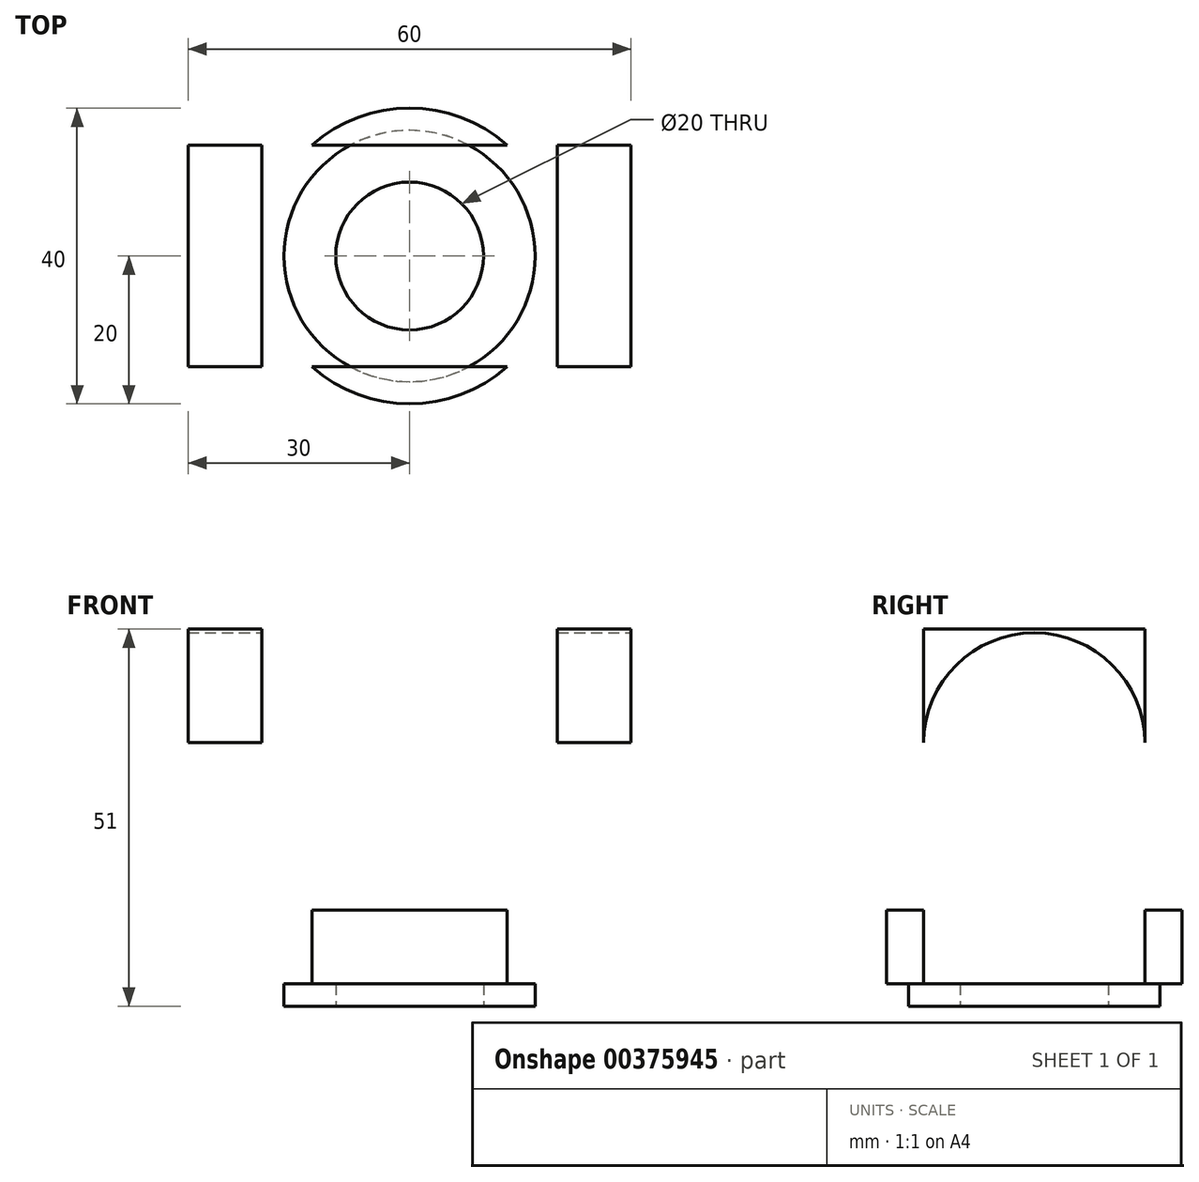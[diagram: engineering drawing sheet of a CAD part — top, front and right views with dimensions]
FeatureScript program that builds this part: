
annotation { "Feature Type Name" : "Feature", "Feature Type Description" : "" }
export const myFeature = defineFeature(function(context is Context, id is Id, definition is map)
    precondition{}
    {
        {
            var Q0;
            Q0=qCreatedBy(makeId("Top.planeOp"),FACE);
            var sketch = newSketch(context, id + "F0", { "sketchPlane" : qUnion([Q0])});
            skCircle(sketch, "E0", {"center": v(0, 0) * mm, "radius": 10 * mm});
            skCircle(sketch, "E1", {"center": v(0, 0) * mm, "radius": 20 * mm});
            skLineSegment(sketch, "E2.bottom", {"start": v(30, 15) * mm, "end": v(-30, 15) * mm});
            skLineSegment(sketch, "E2.top", {"start": v(30, -15) * mm, "end": v(-30, -15) * mm});
            skLineSegment(sketch, "E2.left", {"start": v(30, 15) * mm, "end": v(30, -15) * mm});
            skLineSegment(sketch, "E2.right", {"start": v(-30, 15) * mm, "end": v(-30, -15) * mm});
            skCircle(sketch, "E3", {"center": v(0, 0) * mm, "radius": 17 * mm});
            skSolve(sketch);
        }
        {
            var Q0;
            {var subQ5=sQuery(id+"F0.wireOp",EDGE,"E2.left");Q0=makeQuery(id+"F0.imprint","IMPRINT",FACE,{"disambiguationData":[TD([[makeQuery(id+"F0.imprint","IMPRINT",EDGE,{"derivedFrom":subQ5}),-1.0]])]});}
            var Q1;
            {var subQ5=sQuery(id+"F0.wireOp",EDGE,"E2.right");Q1=makeQuery(id+"F0.imprint","IMPRINT",FACE,{"disambiguationData":[TD([[makeQuery(id+"F0.imprint","IMPRINT",EDGE,{"derivedFrom":subQ5}),1.0]])]});}
            var Q2;
            {var subQ0=sQuery(id+"F0.wireOp",EDGE,"E2.bottom");var subQ1=sQuery(id+"F0.wireOp",EDGE,"E1");var subQ2=makeQuery(id+"F0.imprint","INTERSECT",VERTEX,{"disambiguationData":[OD(0.0)],"derivedFrom":[subQ1,subQ0]});Q2=makeQuery(id+"F0.imprint","IMPRINT",FACE,{"disambiguationData":[TD([[makeQuery(id+"F0.imprint","IMPRINT",EDGE,{"disambiguationData":[TD([[subQ2,1.0]])],"derivedFrom":subQ1}),1.0]])]});}
            var Q3;
            {var subQ0=sQuery(id+"F0.wireOp",EDGE,"E2.top");var subQ1=sQuery(id+"F0.wireOp",EDGE,"E1");var subQ2=makeQuery(id+"F0.imprint","INTERSECT",VERTEX,{"disambiguationData":[OD(0.0)],"derivedFrom":[subQ1,subQ0]});Q3=makeQuery(id+"F0.imprint","IMPRINT",FACE,{"disambiguationData":[TD([[makeQuery(id+"F0.imprint","IMPRINT",EDGE,{"disambiguationData":[TD([[subQ2,-1.0]])],"derivedFrom":subQ1}),1.0]])]});}
            var Q4;
            {var subQ0=sQuery(id+"F0.wireOp",EDGE,"E2.bottom");var subQ1=sQuery(id+"F0.wireOp",EDGE,"E1");var subQ2=makeQuery(id+"F0.imprint","INTERSECT",VERTEX,{"disambiguationData":[OD(1.0)],"derivedFrom":[subQ1,subQ0]});Q4=makeQuery(id+"F0.imprint","IMPRINT",FACE,{"disambiguationData":[TD([[makeQuery(id+"F0.imprint","IMPRINT",EDGE,{"disambiguationData":[TD([[subQ2,1.0]])],"derivedFrom":subQ1}),1.0]])]});}
            var Q5;
            {var subQ0=sQuery(id+"F0.wireOp",EDGE,"E2.bottom");var subQ1=sQuery(id+"F0.wireOp",EDGE,"E1");var subQ2=makeQuery(id+"F0.imprint","INTERSECT",VERTEX,{"disambiguationData":[OD(0.0)],"derivedFrom":[subQ1,subQ0]});Q5=makeQuery(id+"F0.imprint","IMPRINT",FACE,{"disambiguationData":[TD([[makeQuery(id+"F0.imprint","IMPRINT",EDGE,{"disambiguationData":[TD([[subQ2,-1.0]])],"derivedFrom":subQ1}),1.0]])]});}
            var Q6;
            Q6=makeQuery(id+"F0.imprint","IMPRINT",FACE,{"disambiguationData":[TD([[makeQuery(id+"F0.imprint","IMPRINT",EDGE,{"derivedFrom":sQuery(id+"F0.wireOp",EDGE,"E0")}),-1.0]])]});
            var Q7;
            {var subQ0=sQuery(id+"F0.wireOp",EDGE,"E3");var subQ1=sQuery(id+"F0.wireOp",EDGE,"E2.bottom");var subQ2=makeQuery(id+"F0.imprint","INTERSECT",VERTEX,{"disambiguationData":[OD(0.0)],"derivedFrom":[subQ1,subQ0]});Q7=makeQuery(id+"F0.imprint","IMPRINT",FACE,{"disambiguationData":[TD([[makeQuery(id+"F0.imprint","IMPRINT",EDGE,{"disambiguationData":[TD([[subQ2,-1.0]])],"derivedFrom":subQ1}),-1.0]])]});}
            var Q8;
            {var subQ0=sQuery(id+"F0.wireOp",EDGE,"E3");var subQ1=sQuery(id+"F0.wireOp",EDGE,"E2.top");var subQ2=makeQuery(id+"F0.imprint","INTERSECT",VERTEX,{"disambiguationData":[OD(0.0)],"derivedFrom":[subQ1,subQ0]});Q8=makeQuery(id+"F0.imprint","IMPRINT",FACE,{"disambiguationData":[TD([[makeQuery(id+"F0.imprint","IMPRINT",EDGE,{"disambiguationData":[TD([[subQ2,-1.0]])],"derivedFrom":subQ1}),1.0]])]});}
            extrude(context, id + "F1", {"entities" : qUnion([Q0, Q1, Q2, Q3, Q4, Q5, Q6, Q7, Q8]), "depth" : 10 * mm});
        }
        {
            var Q0;
            Q0=makeQuery(id+"F0.imprint","IMPRINT",FACE,{"disambiguationData":[TD([[makeQuery(id+"F0.imprint","IMPRINT",EDGE,{"derivedFrom":sQuery(id+"F0.wireOp",EDGE,"E0")}),-1.0]])]});
            var Q1;
            {var subQ0=sQuery(id+"F0.wireOp",EDGE,"E3");var subQ1=sQuery(id+"F0.wireOp",EDGE,"E2.top");var subQ2=makeQuery(id+"F0.imprint","INTERSECT",VERTEX,{"disambiguationData":[OD(0.0)],"derivedFrom":[subQ1,subQ0]});Q1=makeQuery(id+"F0.imprint","IMPRINT",FACE,{"disambiguationData":[TD([[makeQuery(id+"F0.imprint","IMPRINT",EDGE,{"disambiguationData":[TD([[subQ2,-1.0]])],"derivedFrom":subQ1}),1.0]])]});}
            var Q2;
            {var subQ0=sQuery(id+"F0.wireOp",EDGE,"E3");var subQ1=sQuery(id+"F0.wireOp",EDGE,"E2.bottom");var subQ2=makeQuery(id+"F0.imprint","INTERSECT",VERTEX,{"disambiguationData":[OD(0.0)],"derivedFrom":[subQ1,subQ0]});Q2=makeQuery(id+"F0.imprint","IMPRINT",FACE,{"disambiguationData":[TD([[makeQuery(id+"F0.imprint","IMPRINT",EDGE,{"disambiguationData":[TD([[subQ2,-1.0]])],"derivedFrom":subQ1}),-1.0]])]});}
            extrude(context, id + "F2", {"entities" : qUnion([Q0, Q1, Q2]), "operationType" : NewBodyOperationType.ADD, "oppositeDirection" : true, "depth" : 3 * mm});
        }
        {
            var Q0;
            Q0=makeQuery(id+"F1.opExtrude","CAP_FACE",FACE,{"disambiguationData":[OSD([sQuery(id+"F0.wireOp",EDGE,"E0"),sQuery(id+"F0.wireOp",EDGE,"E1"),sQuery(id+"F0.wireOp",EDGE,"E2.bottom"),sQuery(id+"F0.wireOp",EDGE,"E2.top"),sQuery(id+"F0.wireOp",EDGE,"E2.left"),sQuery(id+"F0.wireOp",EDGE,"E2.right")])],"isStart":false});
            var sketch = newSketch(context, id + "F3", { "sketchPlane" : qUnion([Q0])});
            skLineSegment(sketch, "E4.bottom", {"start": v(-30, 15) * mm, "end": v(-20, 15) * mm});
            skLineSegment(sketch, "E4.top", {"start": v(-30, -15) * mm, "end": v(-20, -15) * mm});
            skLineSegment(sketch, "E4.left", {"start": v(-30, 15) * mm, "end": v(-30, -15) * mm});
            skLineSegment(sketch, "E4.right", {"start": v(-20, 15) * mm, "end": v(-20, -15) * mm});
            skLineSegment(sketch, "E5.bottom", {"start": v(30, 15) * mm, "end": v(20, 15) * mm});
            skLineSegment(sketch, "E5.top", {"start": v(30, -15) * mm, "end": v(20, -15) * mm});
            skLineSegment(sketch, "E5.left", {"start": v(30, 15) * mm, "end": v(30, -15) * mm});
            skLineSegment(sketch, "E5.right", {"start": v(20, 15) * mm, "end": v(20, -15) * mm});
            skSolve(sketch);
        }
        {
            var Q0;
            Q0=makeQuery(id+"F3.imprint","IMPRINT",FACE,{"disambiguationData":[TD([[makeQuery(id+"F3.imprint","IMPRINT",EDGE,{"derivedFrom":sQuery(id+"F3.wireOp",EDGE,"E4.bottom")}),1.0]])]});
            var Q1;
            Q1=makeQuery(id+"F3.imprint","IMPRINT",FACE,{"disambiguationData":[TD([[makeQuery(id+"F3.imprint","IMPRINT",EDGE,{"derivedFrom":sQuery(id+"F3.wireOp",EDGE,"E5.bottom")}),1.0]])]});
            extrude(context, id + "F4", {"entities" : qUnion([Q0, Q1]), "operationType" : NewBodyOperationType.ADD, "depth" : 38 * mm});
        }
        {
            var Q0;
            Q0=makeQuery(id+"F4.boolean.opBoolean","MERGE",FACE,{"derivedFrom":[makeQuery(id+"F1.opExtrude","SWEPT_FACE",FACE,{"disambiguationData":[OSD([sQuery(id+"F0.wireOp",EDGE,"E2.left")])]}),makeQuery(id+"F4.opExtrude","SWEPT_FACE",FACE,{"disambiguationData":[OSD([sQuery(id+"F3.wireOp",EDGE,"E5.left")])]})]});
            var sketch = newSketch(context, id + "F5", { "sketchPlane" : qUnion([Q0])});
            skLineSegment(sketch, "E6", {"start": v(-15, 48) * mm, "end": v(0, 48) * mm, "construction": true});
            skLineSegment(sketch, "E7", {"start": v(0, 48) * mm, "end": v(0, 32.5) * mm, "construction": true});
            skCircle(sketch, "E8", {"center": v(0, 32.5) * mm, "radius": 5 * mm});
            skSolve(sketch);
        }
        {
            var Q0;
            Q0=makeQuery(id+"F5.imprint","IMPRINT",FACE,{"disambiguationData":[TD([[makeQuery(id+"F5.imprint","IMPRINT",EDGE,{"derivedFrom":sQuery(id+"F5.wireOp",EDGE,"E8")}),1.0]])]});
            extrude(context, id + "F6", {"entities" : qUnion([Q0]), "operationType" : NewBodyOperationType.REMOVE, "oppositeDirection" : true, "depth" : 75 * mm});
        }
        {
            var Q0;
            Q0=makeQuery(id+"F4.boolean.opBoolean","MERGE",FACE,{"derivedFrom":[makeQuery(id+"F1.opExtrude","SWEPT_FACE",FACE,{"disambiguationData":[OSD([sQuery(id+"F0.wireOp",EDGE,"E2.left")])]}),makeQuery(id+"F4.opExtrude","SWEPT_FACE",FACE,{"disambiguationData":[OSD([sQuery(id+"F3.wireOp",EDGE,"E5.left")])]})]});
            var sketch = newSketch(context, id + "F7", { "sketchPlane" : qUnion([Q0])});
            skArc(sketch, "E9", {"start": v(-15, 32.68) * mm, "mid": v(0, 47.5) * mm, "end": v(15, 32.68) * mm});
            skSolve(sketch);
        }
        {
            var Q0;
            {var subQ0=sQuery(id+"F7.wireOp",EDGE,"E9");Q0=makeQuery(id+"F7.imprint","IMPRINT",FACE,{"disambiguationData":[TD([[makeQuery(id+"F7.imprint","IMPRINT",EDGE,{"derivedFrom":subQ0}),1.0]])]});}
            extrude(context, id + "F8", {"entities" : qUnion([Q0]), "operationType" : NewBodyOperationType.REMOVE, "oppositeDirection" : true, "depth" : 75 * mm});
        }
    });
